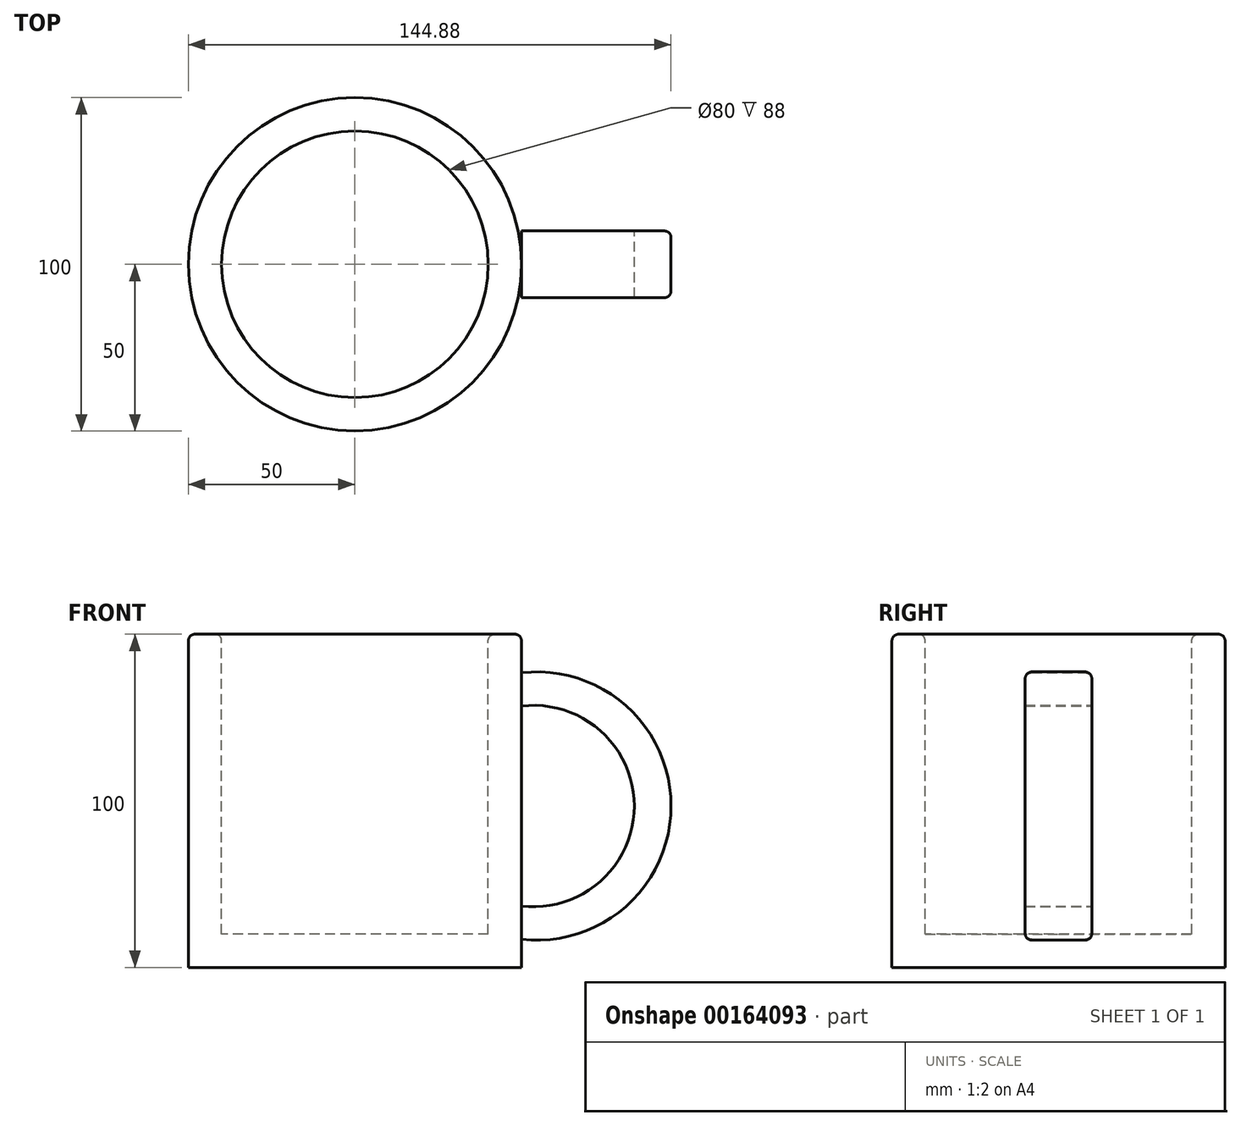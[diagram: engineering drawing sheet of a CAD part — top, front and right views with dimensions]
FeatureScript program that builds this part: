
annotation { "Feature Type Name" : "Feature", "Feature Type Description" : "" }
export const myFeature = defineFeature(function(context is Context, id is Id, definition is map)
    precondition{}
    {
        {
            var Q0;
            Q0=qCreatedBy(makeId("Front.planeOp"),FACE);
            var sketch = newSketch(context, id + "F0", { "sketchPlane" : qUnion([Q0])});
            skLineSegment(sketch, "E0", {"start": v(0, 0) * mm, "end": v(0, 100) * mm});
            skLineSegment(sketch, "E1", {"start": v(0, 100) * mm, "end": v(-10, 100) * mm});
            skLineSegment(sketch, "E2", {"start": v(-10, 100) * mm, "end": v(-10, 10) * mm});
            skLineSegment(sketch, "E3", {"start": v(-10, 10) * mm, "end": v(-50, 10) * mm});
            skLineSegment(sketch, "E4", {"start": v(-50, 10) * mm, "end": v(-50, 0) * mm});
            skLineSegment(sketch, "E5", {"start": v(-50, 0) * mm, "end": v(0, 0) * mm});
            skSolve(sketch);
        }
        {
            var Q0;
            Q0 = qSketchRegion(id + "F0", true);
            var Q1;
            Q1=sQuery(id+"F0.wireOp",EDGE,"E4");
            revolve(context, id + "F1", {"entities" : qUnion([Q0]), "axis" : qUnion([Q1]), "revolveType" : RevolveType.FULL});
        }
        {
            var Q0;
            Q0=qCreatedBy(makeId("Front.planeOp"),FACE);
            var sketch = newSketch(context, id + "F2", { "sketchPlane" : qUnion([Q0])});
            skLineSegment(sketch, "E6", {"start": v(0, 8.42) * mm, "end": v(0, 18.42) * mm});
            skLineSegment(sketch, "E7", {"start": v(0, 88.42) * mm, "end": v(0, 78.42) * mm});
            skArc(sketch, "E8", {"start": v(0, 8.42) * mm, "mid": v(44.88, 48.42) * mm, "end": v(0, 88.42) * mm});
            skArc(sketch, "E9", {"start": v(0, 18.42) * mm, "mid": v(33.84, 48.42) * mm, "end": v(0, 78.42) * mm});
            skSolve(sketch);
        }
        {
            var Q0;
            Q0=makeQuery(id+"F2.imprint","IMPRINT",FACE,{"disambiguationData":[TD([[makeQuery(id+"F2.imprint","IMPRINT",EDGE,{"derivedFrom":sQuery(id+"F2.wireOp",EDGE,"E6")}),-1.0]])]});
            extrude(context, id + "F3", {"entities" : qUnion([Q0]), "operationType" : NewBodyOperationType.ADD, "depth" : 10 * mm});
        }
        {
            var Q0;
            Q0=makeQuery(id+"F2.imprint","IMPRINT",FACE,{"disambiguationData":[TD([[makeQuery(id+"F2.imprint","IMPRINT",EDGE,{"derivedFrom":sQuery(id+"F2.wireOp",EDGE,"E6")}),-1.0]])]});
            extrude(context, id + "F4", {"entities" : qUnion([Q0]), "operationType" : NewBodyOperationType.ADD, "oppositeDirection" : true, "depth" : 10 * mm});
        }
        {
            var Q0;
            Q0=makeQuery(id+"F1.opRevolve","SWEPT_EDGE",EDGE,{"disambiguationData":[OSD([sQuery(id+"F0.wireOp",EDGE,"E1"),sQuery(id+"F0.wireOp",EDGE,"E0")])]});
            var Q1;
            Q1=makeQuery(id+"F1.opRevolve","SWEPT_EDGE",EDGE,{"disambiguationData":[OSD([sQuery(id+"F0.wireOp",EDGE,"E1"),sQuery(id+"F0.wireOp",EDGE,"E2")])]});
            fillet(context, id + "F5", {"entities" : qUnion([Q0, Q1]), "radius" : 2 * mm, "tangentPropagation" : true, "allowEdgeOverflow" : false});
        }
        {
            var Q0;
            Q0=makeQuery(id+"F3.opExtrude","CAP_EDGE",EDGE,{"disambiguationData":[OSD([sQuery(id+"F2.wireOp",EDGE,"E8")])],"isStart":false});
            var Q1;
            Q1=makeQuery(id+"F4.opExtrude","CAP_EDGE",EDGE,{"disambiguationData":[OSD([sQuery(id+"F2.wireOp",EDGE,"E8")])],"isStart":false});
            fillet(context, id + "F6", {"entities" : qUnion([Q0, Q1]), "radius" : 2 * mm, "tangentPropagation" : true, "allowEdgeOverflow" : false});
        }
    });
